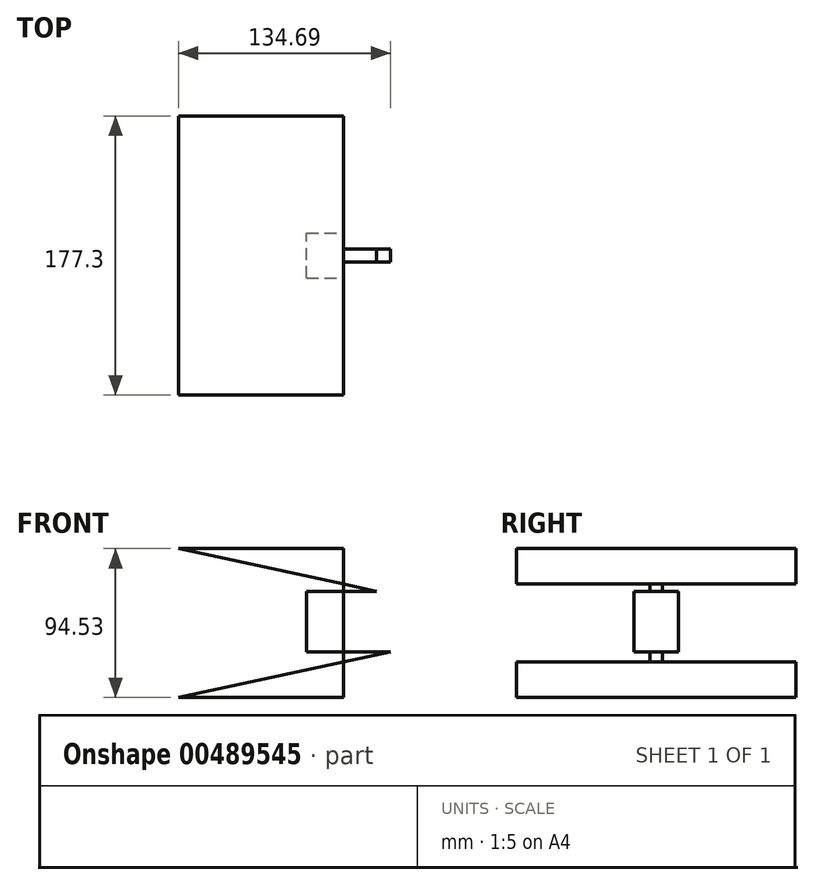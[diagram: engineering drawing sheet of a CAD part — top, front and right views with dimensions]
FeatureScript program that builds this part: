
annotation { "Feature Type Name" : "Feature", "Feature Type Description" : "" }
export const myFeature = defineFeature(function(context is Context, id is Id, definition is map)
    precondition{}
    {
        {
            var Q0;
            Q0=qCreatedBy(makeId("Front.planeOp"),FACE);
            var sketch = newSketch(context, id + "F0", { "sketchPlane" : qUnion([Q0])});
            skLineSegment(sketch, "E0.bottom", {"start": v(11.68, -19.24) * mm, "end": v(-11.68, -19.24) * mm});
            skLineSegment(sketch, "E0.top", {"start": v(-11.68, 19.24) * mm, "end": v(11.68, 19.24) * mm});
            skLineSegment(sketch, "E0.left", {"start": v(-11.68, 19.24) * mm, "end": v(-11.68, -19.24) * mm});
            skLineSegment(sketch, "E0.right", {"start": v(11.68, 19.24) * mm, "end": v(11.68, -19.24) * mm});
            skPoint(sketch, "E0.middle", {"position": v(0, 0) * mm});
            skLineSegment(sketch, "E1", {"start": v(11.68, -48.22) * mm, "end": v(11.68, -19.24) * mm});
            skPoint(sketch, "E1.endSnap0", {"position": v(11.68, 0) * mm});
            skLineSegment(sketch, "E2", {"start": v(11.68, -48.22) * mm, "end": v(-92.97, -48.22) * mm});
            skLineSegment(sketch, "E3", {"start": v(-92.97, -48.22) * mm, "end": v(41.72, -19.24) * mm});
            skLineSegment(sketch, "E4", {"start": v(41.72, -19.24) * mm, "end": v(-11.68, -19.24) * mm});
            skLineSegment(sketch, "E5", {"start": v(11.68, 19.24) * mm, "end": v(11.68, 46.3) * mm});
            skLineSegment(sketch, "E6", {"start": v(11.68, 46.3) * mm, "end": v(-92.97, 46.3) * mm});
            skLineSegment(sketch, "E7", {"start": v(32.83, 19.24) * mm, "end": v(-11.68, 19.24) * mm});
            skLineSegment(sketch, "E8", {"start": v(32.83, 19.24) * mm, "end": v(-92.97, 46.3) * mm});
            skSolve(sketch);
        }
        {
            var Q0;
            {var subQ0=sQuery(id+"F0.wireOp",EDGE,"E0.left");Q0=makeQuery(id+"F0.imprint","IMPRINT",FACE,{"disambiguationData":[TD([[makeQuery(id+"F0.imprint","IMPRINT",EDGE,{"derivedFrom":subQ0}),1.0]])]});}
            extrude(context, id + "F1", {"entities" : qUnion([Q0]), "depth" : 28.45 * mm, "symmetric" : true});
        }
        {
            var Q0;
            {var subQ0=sQuery(id+"F0.wireOp",EDGE,"E2");Q0=makeQuery(id+"F0.imprint","IMPRINT",FACE,{"disambiguationData":[TD([[makeQuery(id+"F0.imprint","IMPRINT",EDGE,{"derivedFrom":subQ0}),-1.0]])]});}
            var Q1;
            {var subQ0=sQuery(id+"F0.wireOp",EDGE,"E6");Q1=makeQuery(id+"F0.imprint","IMPRINT",FACE,{"disambiguationData":[TD([[makeQuery(id+"F0.imprint","IMPRINT",EDGE,{"derivedFrom":subQ0}),1.0]])]});}
            extrude(context, id + "F2", {"entities" : qUnion([Q0, Q1]), "depth" : 177.3 * mm, "symmetric" : true});
        }
        {
            var Q0;
            {var subQ0=sQuery(id+"F0.wireOp",EDGE,"E4");var subQ3=sQuery(id+"F0.wireOp",EDGE,"E3");var subQ5=makeQuery(id+"F0.imprint","INTERSECT",VERTEX,{"derivedFrom":[subQ3,subQ0]});Q0=makeQuery(id+"F0.imprint","IMPRINT",FACE,{"disambiguationData":[TD([[makeQuery(id+"F0.imprint","IMPRINT",EDGE,{"disambiguationData":[TD([[subQ5,1.0]])],"derivedFrom":subQ3}),1.0]])]});}
            var Q1;
            {var subQ0=sQuery(id+"F0.wireOp",EDGE,"E7");var subQ3=sQuery(id+"F0.wireOp",EDGE,"E8");var subQ5=makeQuery(id+"F0.imprint","INTERSECT",VERTEX,{"derivedFrom":[subQ0,subQ3]});Q1=makeQuery(id+"F0.imprint","IMPRINT",FACE,{"disambiguationData":[TD([[makeQuery(id+"F0.imprint","IMPRINT",EDGE,{"disambiguationData":[TD([[subQ5,-1.0]])],"derivedFrom":subQ3}),1.0]])]});}
            extrude(context, id + "F3", {"entities" : qUnion([Q0, Q1]), "depth" : 8.13 * mm, "symmetric" : true});
        }
    });
